# Revit family: Mechanical_Menzies-Metal_Built-Up-Roof-Vent (1)
name_source: partatom
category: Mechanical Equipment
revit_build: Autodesk Revit 2018 (Build: 20170223_1515(x64)
units: mm (PartAtom-declared; Revit-internal decimal feet)

## family parameters
Cut with Voids When Loaded = No
Host = Face
OmniClass Number = 23.70.50.21.24.11
OmniClass Title = Roof Waste Water Drains
Part Type = Normal
Room Calculation Point = No
Round Connector Dimension = Use Diameter
Shared = No

## types (6) — shared parameters
Assembly Code = D2040200
Default Elevation = 48 "
Description = Built Up Roof Vent
Drain Flow = 0 GPM
Edition number = 1
Manufacturer = Menzies Metal Products
Product Guid = 63ebfbcc-aa18-4306-9995-e50899f83029
Product Material = Metal - Menzies Metal Products - Galvanized Steel
Product data url = https://www.bimobject.com
URL = https://www.menzies-metal.com

## per-type parameters (varying)
| type | CW Connection | Depth | HW Connection | Model | Vent Connection | Waste Connection | Weight | Width |
| 5 x 14 | Yes | 5 " | Yes | 600-2110HW | Yes | Yes | 4.40 lbf | 14 " |
| 5 x 20 | No | 5 " | No | 600-2115HW | No | No | 6.50 lbf | 20 " |
| 12 x 12 | No | 12 " | No | 600-2105HW | No | No | 6.80 lbf | 12 " |
| 6 x 6 | No | 6 " | No | 600-2103HW | No | No | 3.60 lbf | 6 " |
| 8 x 8 | Yes | 8 " | Yes | 600-2100HW | Yes | Yes | 4.35 lbf | 8 " |
| 5 x 24 | No | 5 " | No | 600-2120HW | No | No | 7.75 lbf | 24 " |

## geometry (parser evidence)
native form markers: Sweep x2
no freeform markers — native parametric forms only
